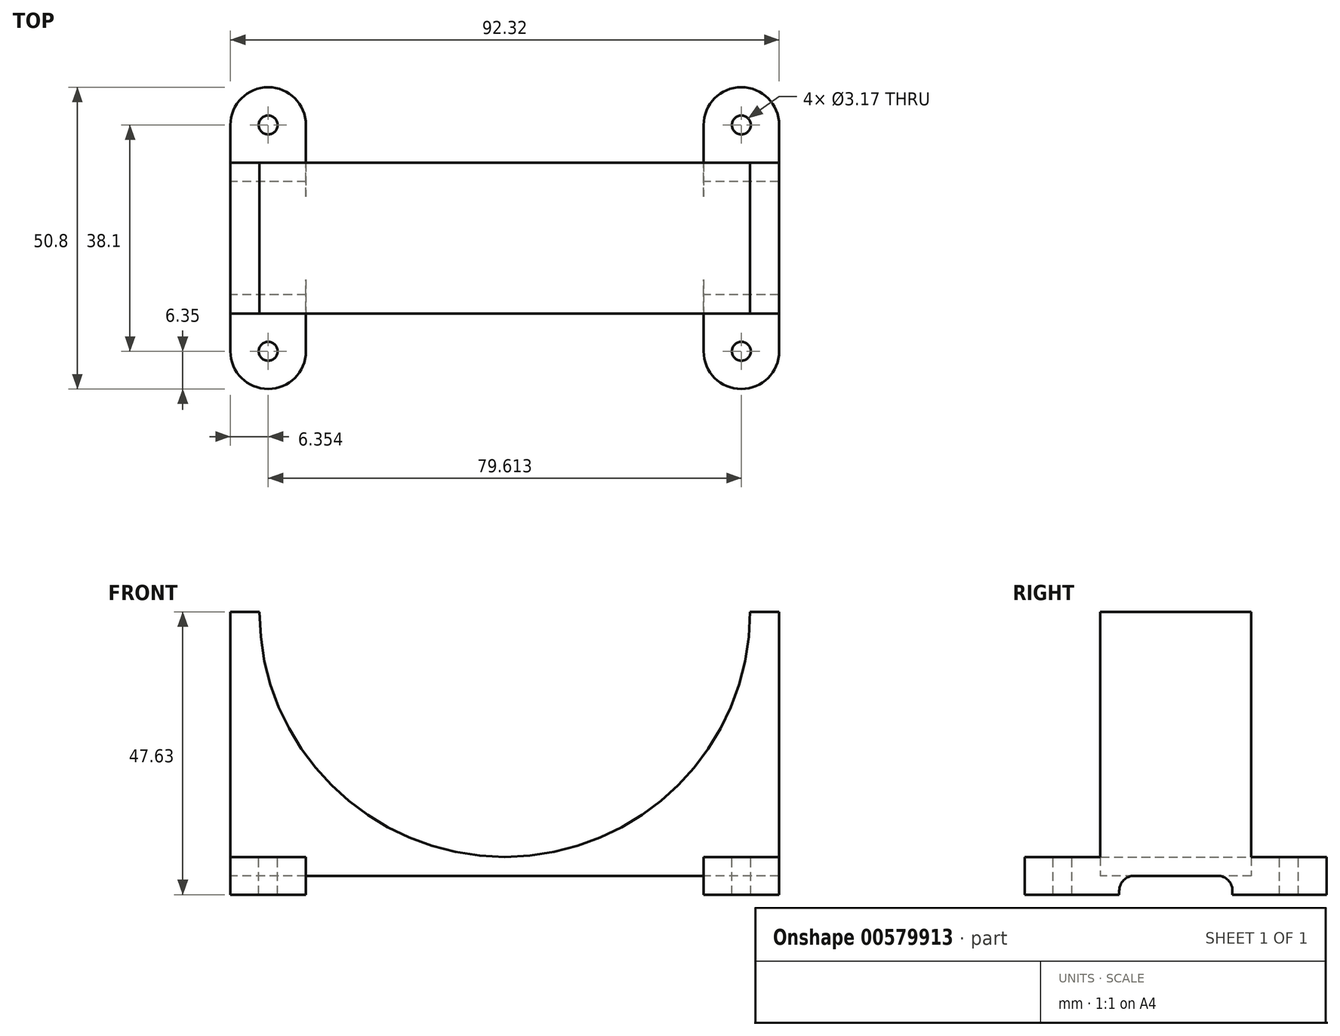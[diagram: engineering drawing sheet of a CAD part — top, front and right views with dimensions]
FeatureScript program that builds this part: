
annotation { "Feature Type Name" : "Feature", "Feature Type Description" : "" }
export const myFeature = defineFeature(function(context is Context, id is Id, definition is map)
    precondition{}
    {
        {
            var Q0;
            Q0=qCreatedBy(makeId("Front.planeOp"),FACE);
            var sketch = newSketch(context, id + "F0", { "sketchPlane" : qUnion([Q0])});
            skArc(sketch, "E0", {"start": v(-41.28, 0) * mm, "mid": v(0, -41.28) * mm, "end": v(41.28, 0) * mm});
            skLineSegment(sketch, "E1", {"start": v(-41.28, 0) * mm, "end": v(-46.16, 0) * mm});
            skLineSegment(sketch, "E2", {"start": v(41.28, 0) * mm, "end": v(46.16, 0) * mm});
            skLineSegment(sketch, "E3", {"start": v(-46.16, 0) * mm, "end": v(-46.16, -47.62) * mm});
            skLineSegment(sketch, "E4", {"start": v(-46.16, -47.62) * mm, "end": v(46.16, -47.62) * mm});
            skLineSegment(sketch, "E5", {"start": v(46.16, -47.62) * mm, "end": v(46.16, 0) * mm});
            skSolve(sketch);
        }
        {
            var Q0;
            Q0 = qSketchRegion(id + "F0", true);
            extrude(context, id + "F1", {"entities" : qUnion([Q0]), "depth" : 25.4 * mm, "offsetDistance" : 25.4 * mm});
        }
        {
            var Q0;
            Q0=makeQuery(id+"F1.opExtrude","CAP_FACE",FACE,{"disambiguationData":[OSD([sQuery(id+"F0.wireOp",EDGE,"E0"),sQuery(id+"F0.wireOp",EDGE,"E1"),sQuery(id+"F0.wireOp",EDGE,"E2"),sQuery(id+"F0.wireOp",EDGE,"E3"),sQuery(id+"F0.wireOp",EDGE,"E4"),sQuery(id+"F0.wireOp",EDGE,"E5")])],"isStart":false});
            var sketch = newSketch(context, id + "F2", { "sketchPlane" : qUnion([Q0])});
            skLineSegment(sketch, "E6.bottom", {"start": v(-46.16, -47.62) * mm, "end": v(-33.46, -47.62) * mm});
            skLineSegment(sketch, "E6.top", {"start": v(-46.16, -41.27) * mm, "end": v(-33.46, -41.27) * mm});
            skLineSegment(sketch, "E6.left", {"start": v(-46.16, -47.62) * mm, "end": v(-46.16, -41.27) * mm});
            skLineSegment(sketch, "E6.right", {"start": v(-33.46, -47.62) * mm, "end": v(-33.46, -41.27) * mm});
            skLineSegment(sketch, "E7.bottom", {"start": v(46.16, -47.62) * mm, "end": v(33.46, -47.62) * mm});
            skLineSegment(sketch, "E7.top", {"start": v(46.16, -41.27) * mm, "end": v(33.46, -41.27) * mm});
            skLineSegment(sketch, "E7.left", {"start": v(46.16, -47.62) * mm, "end": v(46.16, -41.27) * mm});
            skLineSegment(sketch, "E7.right", {"start": v(33.46, -47.62) * mm, "end": v(33.46, -41.27) * mm});
            skSolve(sketch);
        }
        {
            var Q0;
            Q0 = qSketchRegion(id + "F2", true);
            extrude(context, id + "F3", {"entities" : qUnion([Q0]), "operationType" : NewBodyOperationType.ADD, "depth" : 12.7 * mm, "offsetDistance" : 25.4 * mm, "hasSecondDirection" : true, "secondDirectionOppositeDirection" : true, "secondDirectionDepth" : 38.1 * mm});
        }
        {
            var Q0;
            Q0=makeQuery(id+"F3.opExtrude","CAP_EDGE",EDGE,{"disambiguationData":[OSD([sQuery(id+"F2.wireOp",EDGE,"E6.left")])],"isStart":true});
            var Q1;
            Q1=makeQuery(id+"F3.opExtrude","CAP_EDGE",EDGE,{"disambiguationData":[OSD([sQuery(id+"F2.wireOp",EDGE,"E6.right")])],"isStart":true});
            var Q2;
            Q2=makeQuery(id+"F3.opExtrude","CAP_EDGE",EDGE,{"disambiguationData":[OSD([sQuery(id+"F2.wireOp",EDGE,"E6.left")])],"isStart":false});
            var Q3;
            Q3=makeQuery(id+"F3.opExtrude","CAP_EDGE",EDGE,{"disambiguationData":[OSD([sQuery(id+"F2.wireOp",EDGE,"E6.right")])],"isStart":false});
            var Q4;
            Q4=makeQuery(id+"F3.opExtrude","CAP_EDGE",EDGE,{"disambiguationData":[OSD([sQuery(id+"F2.wireOp",EDGE,"E7.right")])],"isStart":false});
            var Q5;
            Q5=makeQuery(id+"F3.opExtrude","CAP_EDGE",EDGE,{"disambiguationData":[OSD([sQuery(id+"F2.wireOp",EDGE,"E7.left")])],"isStart":false});
            var Q6;
            Q6=makeQuery(id+"F3.opExtrude","CAP_EDGE",EDGE,{"disambiguationData":[OSD([sQuery(id+"F2.wireOp",EDGE,"E7.right")])],"isStart":true});
            var Q7;
            Q7=makeQuery(id+"F3.opExtrude","CAP_EDGE",EDGE,{"disambiguationData":[OSD([sQuery(id+"F2.wireOp",EDGE,"E7.left")])],"isStart":true});
            fillet(context, id + "F4", {"entities" : qUnion([Q0, Q1, Q2, Q3, Q4, Q5, Q6, Q7]), "radius" : 6.35 * mm, "tangentPropagation" : true, "allowEdgeOverflow" : false});
        }
        {
            var Q0;
            Q0=makeQuery(id+"F3.boolean.opBoolean","MERGE",FACE,{"derivedFrom":[makeQuery(id+"F1.opExtrude","SWEPT_FACE",FACE,{"disambiguationData":[OSD([sQuery(id+"F0.wireOp",EDGE,"E3")])]}),makeQuery(id+"F3.opExtrude","SWEPT_FACE",FACE,{"disambiguationData":[OSD([sQuery(id+"F2.wireOp",EDGE,"E6.left")])]})]});
            var sketch = newSketch(context, id + "F5", { "sketchPlane" : qUnion([Q0])});
            skLineSegment(sketch, "E8.bottom", {"start": v(3.18, -47.62) * mm, "end": v(22.23, -47.62) * mm});
            skLineSegment(sketch, "E8.top", {"start": v(3.18, -44.45) * mm, "end": v(22.23, -44.45) * mm});
            skLineSegment(sketch, "E8.left", {"start": v(3.18, -47.62) * mm, "end": v(3.18, -44.45) * mm});
            skLineSegment(sketch, "E8.right", {"start": v(22.23, -47.62) * mm, "end": v(22.23, -44.45) * mm});
            skSolve(sketch);
        }
        {
            var Q0;
            Q0 = qSketchRegion(id + "F5", true);
            extrude(context, id + "F6", {"entities" : qUnion([Q0]), "operationType" : NewBodyOperationType.REMOVE, "endBound" : BoundingType.THROUGH_ALL, "oppositeDirection" : true, "depth" : 25.4 * mm, "offsetDistance" : 25.4 * mm});
        }
        {
            var Q0;
            Q0=makeQuery(id+"F1.opExtrude","CAP_FACE",FACE,{"disambiguationData":[OSD([sQuery(id+"F0.wireOp",EDGE,"E0"),sQuery(id+"F0.wireOp",EDGE,"E1"),sQuery(id+"F0.wireOp",EDGE,"E2"),sQuery(id+"F0.wireOp",EDGE,"E3"),sQuery(id+"F0.wireOp",EDGE,"E4"),sQuery(id+"F0.wireOp",EDGE,"E5")])],"isStart":false});
            var sketch = newSketch(context, id + "F7", { "sketchPlane" : qUnion([Q0])});
            skLineSegment(sketch, "E9.bottom", {"start": v(-33.46, -47.62) * mm, "end": v(33.46, -47.62) * mm});
            skLineSegment(sketch, "E9.top", {"start": v(-33.46, -44.45) * mm, "end": v(33.46, -44.45) * mm});
            skLineSegment(sketch, "E9.left", {"start": v(-33.46, -47.62) * mm, "end": v(-33.46, -44.45) * mm});
            skLineSegment(sketch, "E9.right", {"start": v(33.46, -47.62) * mm, "end": v(33.46, -44.45) * mm});
            skSolve(sketch);
        }
        {
            var Q0;
            Q0 = qSketchRegion(id + "F7", true);
            extrude(context, id + "F8", {"entities" : qUnion([Q0]), "operationType" : NewBodyOperationType.REMOVE, "endBound" : BoundingType.THROUGH_ALL, "oppositeDirection" : true, "depth" : 25.4 * mm, "offsetDistance" : 25.4 * mm});
        }
        {
            var Q0;
            {var subQ0=sQuery(id+"F5.wireOp",EDGE,"E8.top");var subQ1=sQuery(id+"F5.wireOp",EDGE,"E8.right");Q0=makeQuery(id+"F8.boolean.opBoolean","SPLIT",EDGE,{"disambiguationData":[TD([makeQuery(id+"F1.opExtrude","SWEPT_FACE",FACE,{"disambiguationData":[OSD([sQuery(id+"F0.wireOp",EDGE,"E3")])]})])],"derivedFrom":makeQuery(id+"F6.boolean.opBoolean","COPY",EDGE,{"derivedFrom":makeQuery(id+"F6.opExtrude","SWEPT_EDGE",EDGE,{"disambiguationData":[OSD([subQ0,subQ1])]})})});}
            var Q1;
            {var subQ0=sQuery(id+"F5.wireOp",EDGE,"E8.top");var subQ1=sQuery(id+"F5.wireOp",EDGE,"E8.left");Q1=makeQuery(id+"F8.boolean.opBoolean","SPLIT",EDGE,{"disambiguationData":[TD([makeQuery(id+"F1.opExtrude","SWEPT_FACE",FACE,{"disambiguationData":[OSD([sQuery(id+"F0.wireOp",EDGE,"E3")])]})])],"derivedFrom":makeQuery(id+"F6.boolean.opBoolean","COPY",EDGE,{"derivedFrom":makeQuery(id+"F6.opExtrude","SWEPT_EDGE",EDGE,{"disambiguationData":[OSD([subQ0,subQ1])]})})});}
            var Q2;
            {var subQ0=sQuery(id+"F5.wireOp",EDGE,"E8.top");var subQ1=sQuery(id+"F5.wireOp",EDGE,"E8.left");Q2=makeQuery(id+"F8.boolean.opBoolean","SPLIT",EDGE,{"disambiguationData":[TD([makeQuery(id+"F1.opExtrude","SWEPT_FACE",FACE,{"disambiguationData":[OSD([sQuery(id+"F0.wireOp",EDGE,"E5")])]})])],"derivedFrom":makeQuery(id+"F6.boolean.opBoolean","COPY",EDGE,{"derivedFrom":makeQuery(id+"F6.opExtrude","SWEPT_EDGE",EDGE,{"disambiguationData":[OSD([subQ0,subQ1])]})})});}
            var Q3;
            {var subQ0=sQuery(id+"F5.wireOp",EDGE,"E8.top");var subQ1=sQuery(id+"F5.wireOp",EDGE,"E8.right");Q3=makeQuery(id+"F8.boolean.opBoolean","SPLIT",EDGE,{"disambiguationData":[TD([makeQuery(id+"F1.opExtrude","SWEPT_FACE",FACE,{"disambiguationData":[OSD([sQuery(id+"F0.wireOp",EDGE,"E5")])]})])],"derivedFrom":makeQuery(id+"F6.boolean.opBoolean","COPY",EDGE,{"derivedFrom":makeQuery(id+"F6.opExtrude","SWEPT_EDGE",EDGE,{"disambiguationData":[OSD([subQ0,subQ1])]})})});}
            fillet(context, id + "F9", {"entities" : qUnion([Q0, Q1, Q2, Q3]), "radius" : 2.54 * mm, "tangentPropagation" : true, "allowEdgeOverflow" : false});
        }
        {
            var Q0;
            {var subQ0=sQuery(id+"F2.wireOp",EDGE,"E6.right");var subQ1=sQuery(id+"F2.wireOp",EDGE,"E6.left");var subQ2=sQuery(id+"F2.wireOp",EDGE,"E6.top");Q0=makeQuery(id+"F3.boolean.opBoolean","SPLIT",FACE,{"disambiguationData":[TD([makeQuery(id+"F3.opExtrude","CAP_FACE",FACE,{"disambiguationData":[OSD([sQuery(id+"F2.wireOp",EDGE,"E6.bottom"),subQ2,subQ1,subQ0])],"isStart":false})])],"derivedFrom":makeQuery(id+"F3.opExtrude","SWEPT_FACE",FACE,{"disambiguationData":[OSD([subQ2])]})});}
            var sketch = newSketch(context, id + "F10", { "sketchPlane" : qUnion([Q0])});
            skCircle(sketch, "E10", {"center": v(-39.8, -31.75) * mm, "radius": 1.59 * mm});
            skCircle(sketch, "E11", {"center": v(-39.8, 6.35) * mm, "radius": 1.59 * mm});
            skCircle(sketch, "E12.MirrorC", {"center": v(39.8, -31.75) * mm, "radius": 1.59 * mm});
            skCircle(sketch, "E13.MirrorC", {"center": v(39.8, 6.35) * mm, "radius": 1.59 * mm});
            skSolve(sketch);
        }
        {
            var Q0;
            Q0 = qSketchRegion(id + "F10", true);
            extrude(context, id + "F11", {"entities" : qUnion([Q0]), "operationType" : NewBodyOperationType.REMOVE, "endBound" : BoundingType.THROUGH_ALL, "oppositeDirection" : true, "depth" : 25.4 * mm, "offsetDistance" : 25.4 * mm});
        }
    });
